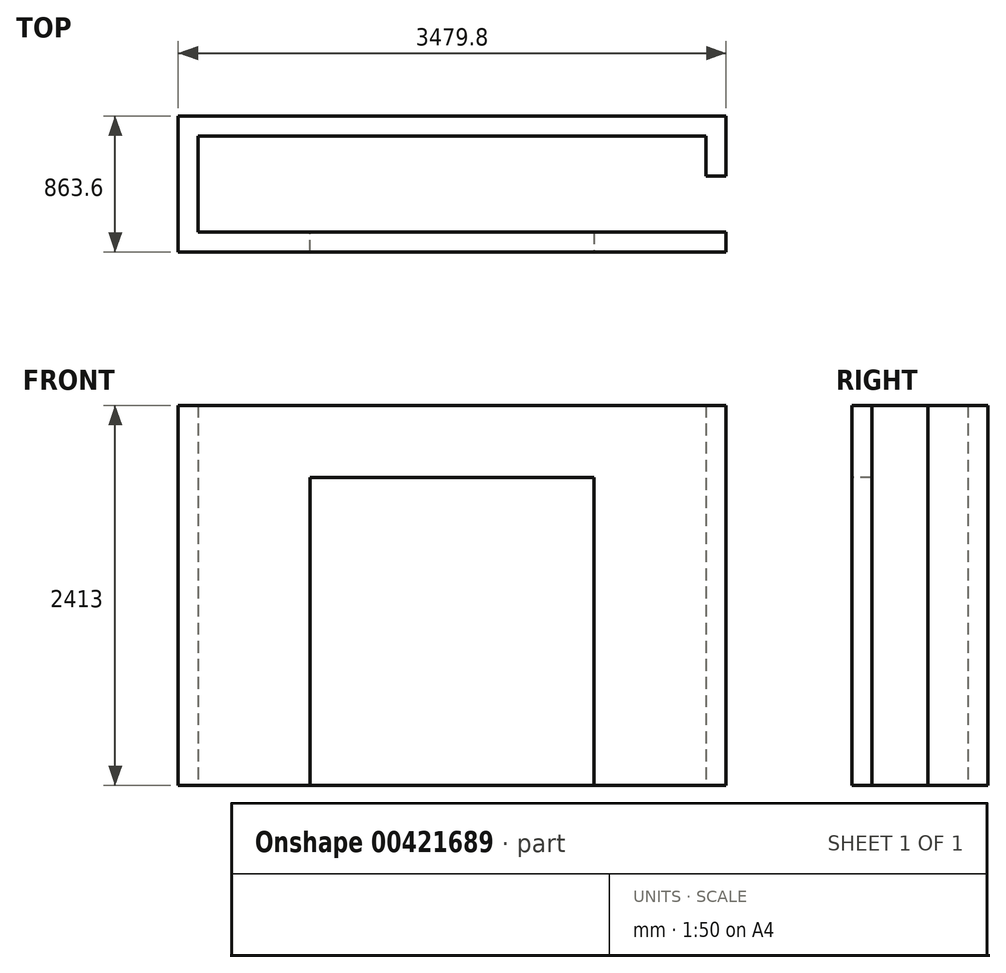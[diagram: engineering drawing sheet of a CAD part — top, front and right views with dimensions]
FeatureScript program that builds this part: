
annotation { "Feature Type Name" : "Feature", "Feature Type Description" : "" }
export const myFeature = defineFeature(function(context is Context, id is Id, definition is map)
    precondition{}
    {
        {
            var Q0;
            Q0=qCreatedBy(makeId("Top.planeOp"),FACE);
            var sketch = newSketch(context, id + "F0", { "sketchPlane" : qUnion([Q0])});
            skLineSegment(sketch, "E0", {"start": v(-1739.9, -127) * mm, "end": v(-901.7, -127) * mm});
            skLineSegment(sketch, "E1", {"start": v(-901.7, -127) * mm, "end": v(-901.7, 0) * mm});
            skLineSegment(sketch, "E2", {"start": v(-901.7, 0) * mm, "end": v(-1612.9, 0) * mm});
            skLineSegment(sketch, "E3", {"start": v(-1612.9, 0) * mm, "end": v(-1612.9, 609.6) * mm});
            skLineSegment(sketch, "E4", {"start": v(-1612.9, 609.6) * mm, "end": v(1612.9, 609.6) * mm});
            skLineSegment(sketch, "E5", {"start": v(1612.9, 609.6) * mm, "end": v(1612.9, 0) * mm});
            skLineSegment(sketch, "E6", {"start": v(1612.9, 0) * mm, "end": v(901.7, 0) * mm});
            skLineSegment(sketch, "E7", {"start": v(901.7, 0) * mm, "end": v(901.7, -127) * mm});
            skLineSegment(sketch, "E8", {"start": v(901.7, -127) * mm, "end": v(1739.9, -127) * mm});
            skLineSegment(sketch, "E9", {"start": v(0, 609.6) * mm, "end": v(0, 0) * mm, "construction": true});
            skLineSegment(sketch, "E10", {"start": v(-1739.9, -127) * mm, "end": v(-1739.9, 736.6) * mm});
            skLineSegment(sketch, "E11", {"start": v(-1739.9, 736.6) * mm, "end": v(1739.9, 736.6) * mm});
            skLineSegment(sketch, "E12", {"start": v(1739.9, 736.6) * mm, "end": v(1739.9, -127) * mm});
            skLineSegment(sketch, "E13", {"start": v(0, 609.6) * mm, "end": v(0, 736.6) * mm, "construction": true});
            skLineSegment(sketch, "E14", {"start": v(1612.9, 355.6) * mm, "end": v(1739.9, 355.6) * mm, "construction": true});
            skSolve(sketch);
        }
        {
            var Q0;
            Q0 = qSketchRegion(id + "F0", true);
            extrude(context, id + "F1", {"entities" : qUnion([Q0]), "depth" : 2413 * mm});
        }
        {
            var Q0;
            Q0=makeQuery(id+"F1.opExtrude","SWEPT_FACE",FACE,{"disambiguationData":[OSD([sQuery(id+"F0.wireOp",EDGE,"E0")])]});
            var sketch = newSketch(context, id + "F2", { "sketchPlane" : qUnion([Q0])});
            skLineSegment(sketch, "E15.bottom", {"start": v(-901.7, 2413) * mm, "end": v(901.7, 2413) * mm});
            skLineSegment(sketch, "E15.top", {"start": v(-901.7, 1955.8) * mm, "end": v(901.7, 1955.8) * mm});
            skLineSegment(sketch, "E15.left", {"start": v(-901.7, 2413) * mm, "end": v(-901.7, 1955.8) * mm});
            skLineSegment(sketch, "E15.right", {"start": v(901.7, 2413) * mm, "end": v(901.7, 1955.8) * mm});
            skSolve(sketch);
        }
        {
            var Q0;
            Q0 = qSketchRegion(id + "F2", true);
            var Q1;
            Q1=makeQuery(id+"F1.opExtrude","SWEPT_FACE",FACE,{"disambiguationData":[OSD([sQuery(id+"F0.wireOp",EDGE,"E2")])]});
            extrude(context, id + "F3", {"entities" : qUnion([Q0]), "operationType" : NewBodyOperationType.ADD, "endBound" : BoundingType.UP_TO_SURFACE, "oppositeDirection" : true, "endBoundEntityFace" : qUnion([Q1]), "depth" : 284.48 * mm});
        }
        {
            var Q0;
            Q0=makeQuery(id+"F3.boolean.opBoolean","MERGE",FACE,{"derivedFrom":[makeQuery(id+"F1.opExtrude","CAP_FACE",FACE,{"disambiguationData":[OSD([sQuery(id+"F0.wireOp",EDGE,"E0"),sQuery(id+"F0.wireOp",EDGE,"E1"),sQuery(id+"F0.wireOp",EDGE,"E2"),sQuery(id+"F0.wireOp",EDGE,"E3"),sQuery(id+"F0.wireOp",EDGE,"E4"),sQuery(id+"F0.wireOp",EDGE,"E5"),sQuery(id+"F0.wireOp",EDGE,"E6"),sQuery(id+"F0.wireOp",EDGE,"E7"),sQuery(id+"F0.wireOp",EDGE,"E8"),sQuery(id+"F0.wireOp",EDGE,"E10"),sQuery(id+"F0.wireOp",EDGE,"E11"),sQuery(id+"F0.wireOp",EDGE,"E12")])],"isStart":false}),makeQuery(id+"F3.opExtrude","SWEPT_FACE",FACE,{"disambiguationData":[OSD([sQuery(id+"F2.wireOp",EDGE,"E15.bottom")])]})]});
            var sketch = newSketch(context, id + "F4", { "sketchPlane" : qUnion([Q0])});
            skLineSegment(sketch, "E16.bottom", {"start": v(1612.9, 355.6) * mm, "end": v(1739.9, 355.6) * mm});
            skLineSegment(sketch, "E16.top", {"start": v(1612.9, 0) * mm, "end": v(1739.9, 0) * mm});
            skLineSegment(sketch, "E16.left", {"start": v(1612.9, 355.6) * mm, "end": v(1612.9, 0) * mm});
            skLineSegment(sketch, "E16.right", {"start": v(1739.9, 355.6) * mm, "end": v(1739.9, 0) * mm});
            skSolve(sketch);
        }
        {
            var Q0;
            Q0 = qSketchRegion(id + "F4", true);
            extrude(context, id + "F5", {"entities" : qUnion([Q0]), "operationType" : NewBodyOperationType.REMOVE, "endBound" : BoundingType.THROUGH_ALL, "oppositeDirection" : true, "depth" : 25.4 * mm});
        }
    });
